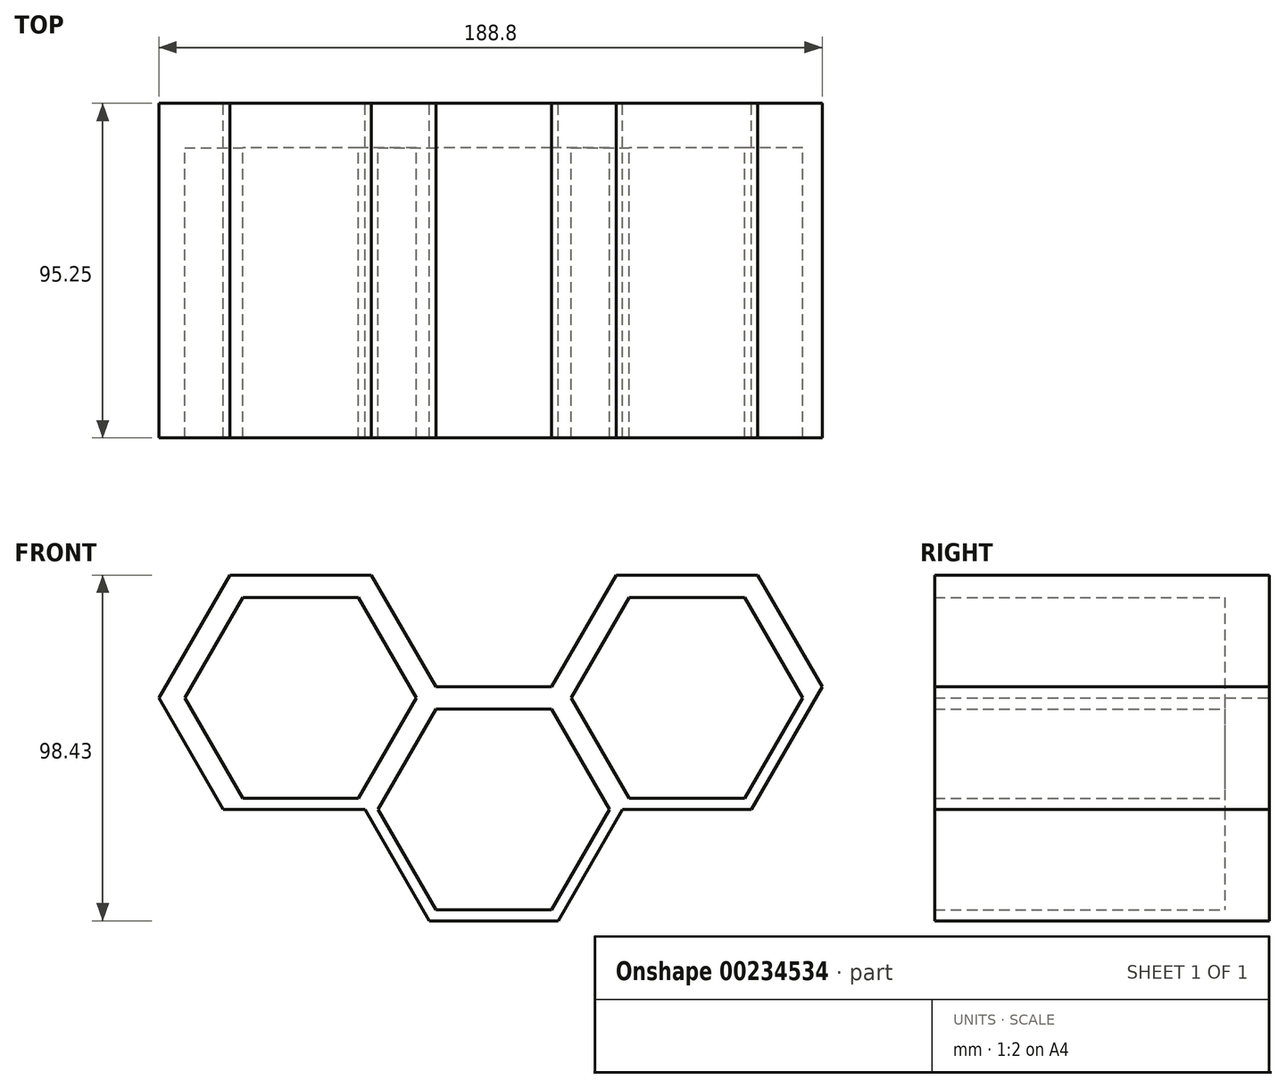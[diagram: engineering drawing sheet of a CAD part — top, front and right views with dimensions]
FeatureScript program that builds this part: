
annotation { "Feature Type Name" : "Feature", "Feature Type Description" : "" }
export const myFeature = defineFeature(function(context is Context, id is Id, definition is map)
    precondition{}
    {
        {
            var Q0;
            Q0=qCreatedBy(makeId("Front.planeOp"),FACE);
            var sketch = newSketch(context, id + "F0", { "sketchPlane" : qUnion([Q0])});
            skLineSegment(sketch, "E0.1", {"start": v(-114.26, 98.54) * mm, "end": v(-77.6, 98.54) * mm});
            skLineSegment(sketch, "E1.1", {"start": v(-169.26, 130.3) * mm, "end": v(-132.6, 130.3) * mm});
            skLineSegment(sketch, "E1.2", {"start": v(-132.6, 130.3) * mm, "end": v(-114.26, 98.54) * mm});
            skLineSegment(sketch, "E2.0", {"start": v(-77.6, 98.54) * mm, "end": v(-59.27, 130.3) * mm});
            skLineSegment(sketch, "E2.1", {"start": v(-59.27, 130.3) * mm, "end": v(-27.5, 130.3) * mm});
            skCircle(sketch, "E3.cCircle", {"center": v(-95.93, 130.3) * mm, "radius": 28.58 * mm, "construction": true});
            skLineSegment(sketch, "E3.0", {"start": v(-128.93, 130.3) * mm, "end": v(-112.43, 158.87) * mm});
            skLineSegment(sketch, "E3.1", {"start": v(-112.43, 158.87) * mm, "end": v(-79.43, 158.87) * mm});
            skLineSegment(sketch, "E3.2", {"start": v(-79.43, 158.87) * mm, "end": v(-62.94, 130.3) * mm});
            skLineSegment(sketch, "E3.3", {"start": v(-62.94, 130.3) * mm, "end": v(-79.43, 101.72) * mm});
            skLineSegment(sketch, "E3.4", {"start": v(-79.43, 101.72) * mm, "end": v(-112.43, 101.72) * mm});
            skLineSegment(sketch, "E3.5", {"start": v(-112.43, 101.72) * mm, "end": v(-128.93, 130.3) * mm});
            skPoint(sketch, "E3.0.midPoint", {"position": v(-120.68, 144.58) * mm});
            skCircle(sketch, "E4.cCircle", {"center": v(-95.93, 130.3) * mm, "radius": 31.75 * mm, "construction": true});
            skLineSegment(sketch, "E4.0", {"start": v(-132.6, 130.3) * mm, "end": v(-114.26, 162.04) * mm});
            skLineSegment(sketch, "E4.1", {"start": v(-114.26, 162.04) * mm, "end": v(-77.6, 162.04) * mm});
            skLineSegment(sketch, "E4.2", {"start": v(-77.6, 162.04) * mm, "end": v(-59.27, 130.3) * mm});
            skLineSegment(sketch, "E4.3", {"start": v(-59.27, 130.3) * mm, "end": v(-77.6, 98.54) * mm});
            skLineSegment(sketch, "E4.4", {"start": v(-77.6, 98.54) * mm, "end": v(-114.26, 98.54) * mm});
            skLineSegment(sketch, "E4.5", {"start": v(-114.26, 98.54) * mm, "end": v(-132.6, 130.3) * mm});
            skPoint(sketch, "E4.0.midPoint", {"position": v(-123.43, 146.17) * mm});
            skCircle(sketch, "E5.cCircle", {"center": v(-150.93, 162.04) * mm, "radius": 28.58 * mm, "construction": true});
            skLineSegment(sketch, "E5.0", {"start": v(-183.92, 162.04) * mm, "end": v(-167.42, 190.62) * mm});
            skLineSegment(sketch, "E5.1", {"start": v(-167.42, 190.62) * mm, "end": v(-134.43, 190.62) * mm});
            skLineSegment(sketch, "E5.2", {"start": v(-134.43, 190.62) * mm, "end": v(-117.93, 162.04) * mm});
            skLineSegment(sketch, "E5.3", {"start": v(-117.93, 162.04) * mm, "end": v(-134.43, 133.47) * mm});
            skLineSegment(sketch, "E5.4", {"start": v(-134.43, 133.47) * mm, "end": v(-167.42, 133.47) * mm});
            skLineSegment(sketch, "E5.5", {"start": v(-167.42, 133.47) * mm, "end": v(-183.92, 162.04) * mm});
            skPoint(sketch, "E5.0.midPoint", {"position": v(-175.67, 176.33) * mm});
            skCircle(sketch, "E6.cCircle", {"center": v(-150.93, 162.04) * mm, "radius": 31.75 * mm, "construction": true});
            skLineSegment(sketch, "E6.0", {"start": v(-187.59, 162.04) * mm, "end": v(-169.26, 193.8) * mm});
            skLineSegment(sketch, "E6.1", {"start": v(-169.26, 193.8) * mm, "end": v(-132.6, 193.8) * mm});
            skLineSegment(sketch, "E6.2", {"start": v(-132.6, 193.8) * mm, "end": v(-114.26, 162.04) * mm});
            skLineSegment(sketch, "E6.3", {"start": v(-114.26, 162.04) * mm, "end": v(-132.6, 130.3) * mm});
            skLineSegment(sketch, "E6.4", {"start": v(-132.6, 130.3) * mm, "end": v(-169.26, 130.3) * mm});
            skLineSegment(sketch, "E6.5", {"start": v(-169.26, 130.3) * mm, "end": v(-187.59, 162.04) * mm});
            skPoint(sketch, "E6.0.midPoint", {"position": v(-178.42, 177.92) * mm});
            skCircle(sketch, "E7.cCircle", {"center": v(-40.94, 162.04) * mm, "radius": 28.58 * mm, "construction": true});
            skLineSegment(sketch, "E7.0", {"start": v(-73.94, 162.04) * mm, "end": v(-57.44, 190.62) * mm});
            skLineSegment(sketch, "E7.1", {"start": v(-57.44, 190.62) * mm, "end": v(-24.44, 190.62) * mm});
            skLineSegment(sketch, "E7.2", {"start": v(-24.44, 190.62) * mm, "end": v(-7.94, 162.04) * mm});
            skLineSegment(sketch, "E7.3", {"start": v(-7.94, 162.04) * mm, "end": v(-24.44, 133.47) * mm});
            skLineSegment(sketch, "E7.4", {"start": v(-24.44, 133.47) * mm, "end": v(-57.44, 133.47) * mm});
            skLineSegment(sketch, "E7.5", {"start": v(-57.44, 133.47) * mm, "end": v(-73.94, 162.04) * mm});
            skCircle(sketch, "E8.cCircle", {"center": v(-40.94, 162.04) * mm, "radius": 31.75 * mm, "construction": true});
            skLineSegment(sketch, "E8.0", {"start": v(-77.6, 162.04) * mm, "end": v(-59.27, 193.8) * mm});
            skLineSegment(sketch, "E8.1", {"start": v(-59.27, 193.8) * mm, "end": v(-22.6, 193.8) * mm});
            skLineSegment(sketch, "E8.2", {"start": v(-22.6, 193.8) * mm, "end": v(-4.28, 162.04) * mm});
            skLineSegment(sketch, "E8.3", {"start": v(-4.28, 162.04) * mm, "end": v(-22.6, 130.3) * mm});
            skLineSegment(sketch, "E8.4", {"start": v(-22.6, 130.3) * mm, "end": v(-59.27, 130.3) * mm});
            skLineSegment(sketch, "E8.5", {"start": v(-59.27, 130.3) * mm, "end": v(-77.6, 162.04) * mm});
            skPoint(sketch, "E8.0.midPoint", {"position": v(-68.44, 177.92) * mm});
            skLineSegment(sketch, "E9.0", {"start": v(-22.6, 130.3) * mm, "end": v(-4.28, 162.04) * mm});
            skPoint(sketch, "E9.0.midPoint", {"position": v(-13.44, 146.17) * mm});
            skLineSegment(sketch, "E10", {"start": v(-2.45, 165.22) * mm, "end": v(-20.78, 196.97) * mm});
            skLineSegment(sketch, "E11", {"start": v(-20.78, 196.97) * mm, "end": v(-61.1, 196.97) * mm});
            skLineSegment(sketch, "E12", {"start": v(-61.1, 196.97) * mm, "end": v(-79.43, 165.22) * mm});
            skLineSegment(sketch, "E13", {"start": v(-171.09, 196.97) * mm, "end": v(-191.25, 162.04) * mm});
            skLineSegment(sketch, "E14", {"start": v(-191.25, 162.04) * mm, "end": v(-172.92, 130.3) * mm});
            skLineSegment(sketch, "E15", {"start": v(-171.09, 196.97) * mm, "end": v(-130.76, 196.97) * mm});
            skLineSegment(sketch, "E16", {"start": v(-130.76, 196.97) * mm, "end": v(-112.43, 165.22) * mm});
            skLineSegment(sketch, "E17", {"start": v(-112.43, 165.22) * mm, "end": v(-79.43, 165.22) * mm});
            skLineSegment(sketch, "E18", {"start": v(-57.44, 127.12) * mm, "end": v(-73.94, 98.54) * mm});
            skLineSegment(sketch, "E19", {"start": v(-24.44, 127.12) * mm, "end": v(-57.44, 127.12) * mm});
            skLineSegment(sketch, "E20", {"start": v(-22.6, 130.3) * mm, "end": v(-24.44, 127.12) * mm});
            skLineSegment(sketch, "E21", {"start": v(-73.94, 98.54) * mm, "end": v(-77.6, 98.54) * mm});
            skLineSegment(sketch, "E22", {"start": v(-169.26, 130.3) * mm, "end": v(-172.92, 130.3) * mm});
            skLineSegment(sketch, "E23", {"start": v(-2.45, 165.22) * mm, "end": v(-4.28, 162.04) * mm});
            skSolve(sketch);
        }
        {
            var Q0;
            Q0=makeQuery(id+"F0.imprint","IMPRINT",FACE,{"disambiguationData":[TD([[makeQuery(id+"F0.imprint","IMPRINT",EDGE,{"derivedFrom":sQuery(id+"F0.wireOp",EDGE,"E7.0")}),-1.0]])]});
            var Q1;
            Q1=makeQuery(id+"F0.imprint","IMPRINT",FACE,{"disambiguationData":[TD([[makeQuery(id+"F0.imprint","IMPRINT",EDGE,{"derivedFrom":sQuery(id+"F0.wireOp",EDGE,"ae29455d-c252-400a-b569-c5a1c48e1351.0")}),-1.0]])]});
            var Q2;
            Q2=makeQuery(id+"F0.imprint","IMPRINT",FACE,{"disambiguationData":[TD([[makeQuery(id+"F0.imprint","IMPRINT",EDGE,{"derivedFrom":sQuery(id+"F0.wireOp",EDGE,"cad1e4f3-bd43-45ec-b31a-1d5006939c94.0")}),-1.0]])]});
            var Q3;
            Q3=makeQuery(id+"F0.imprint","IMPRINT",FACE,{"disambiguationData":[TD([[makeQuery(id+"F0.imprint","IMPRINT",EDGE,{"derivedFrom":sQuery(id+"F0.wireOp",EDGE,"b43d4d8c-f78a-4ff8-8565-99a66ce6ec5f.0")}),-1.0]])]});
            var Q4;
            Q4=makeQuery(id+"F0.imprint","IMPRINT",FACE,{"disambiguationData":[TD([[makeQuery(id+"F0.imprint","IMPRINT",EDGE,{"derivedFrom":sQuery(id+"F0.wireOp",EDGE,"8c75d941-d110-4871-aa41-90a72d60fb2b.0")}),-1.0]])]});
            var Q5;
            Q5=makeQuery(id+"F0.imprint","IMPRINT",FACE,{"disambiguationData":[TD([[makeQuery(id+"F0.imprint","IMPRINT",EDGE,{"derivedFrom":sQuery(id+"F0.wireOp",EDGE,"258573fa-3544-418e-8bc5-5d37e5b8ba09.0")}),-1.0]])]});
            var Q6;
            Q6=makeQuery(id+"F0.imprint","IMPRINT",FACE,{"disambiguationData":[TD([[makeQuery(id+"F0.imprint","IMPRINT",EDGE,{"derivedFrom":sQuery(id+"F0.wireOp",EDGE,"0bf0733b-7d93-4c2e-8366-56d2cde24658.0")}),-1.0]])]});
            var Q7;
            Q7=makeQuery(id+"F0.imprint","IMPRINT",FACE,{"disambiguationData":[TD([[makeQuery(id+"F0.imprint","IMPRINT",EDGE,{"derivedFrom":sQuery(id+"F0.wireOp",EDGE,"93717492-86db-456f-ae55-f71e4e93837b.0")}),-1.0]])]});
            var Q8;
            Q8=makeQuery(id+"F0.imprint","IMPRINT",FACE,{"disambiguationData":[TD([[makeQuery(id+"F0.imprint","IMPRINT",EDGE,{"derivedFrom":sQuery(id+"F0.wireOp",EDGE,"f16ea8c9-6b67-4651-8441-f7eb3c0ce7d7.0")}),-1.0]])]});
            var Q9;
            Q9=makeQuery(id+"F0.imprint","IMPRINT",FACE,{"disambiguationData":[TD([[makeQuery(id+"F0.imprint","IMPRINT",EDGE,{"derivedFrom":sQuery(id+"F0.wireOp",EDGE,"E3.0")}),-1.0]])]});
            var Q10;
            Q10=makeQuery(id+"F0.imprint","IMPRINT",FACE,{"disambiguationData":[TD([[makeQuery(id+"F0.imprint","IMPRINT",EDGE,{"derivedFrom":sQuery(id+"F0.wireOp",EDGE,"0a91a14e-ea0c-483f-91eb-c48bd73cb0e6.0")}),-1.0]])]});
            var Q11;
            Q11=makeQuery(id+"F0.imprint","IMPRINT",FACE,{"disambiguationData":[TD([[makeQuery(id+"F0.imprint","IMPRINT",EDGE,{"derivedFrom":sQuery(id+"F0.wireOp",EDGE,"cbfd9497-f7fe-4f18-9288-d90aa8075d81.0")}),-1.0]])]});
            var Q12;
            Q12=makeQuery(id+"F0.imprint","IMPRINT",FACE,{"disambiguationData":[TD([[makeQuery(id+"F0.imprint","IMPRINT",EDGE,{"derivedFrom":sQuery(id+"F0.wireOp",EDGE,"6282d196-dd8f-4bb0-bca4-b9108e277473.0")}),-1.0]])]});
            var Q13;
            Q13=makeQuery(id+"F0.imprint","IMPRINT",FACE,{"disambiguationData":[TD([[makeQuery(id+"F0.imprint","IMPRINT",EDGE,{"derivedFrom":sQuery(id+"F0.wireOp",EDGE,"E5.0")}),-1.0]])]});
            var Q14;
            Q14=makeQuery(id+"F0.imprint","IMPRINT",FACE,{"disambiguationData":[TD([[makeQuery(id+"F0.imprint","IMPRINT",EDGE,{"derivedFrom":sQuery(id+"F0.wireOp",EDGE,"06c29831-6b25-410b-9247-4ee044b7735c.0")}),-1.0]])]});
            var Q15;
            Q15=makeQuery(id+"F0.imprint","IMPRINT",FACE,{"disambiguationData":[TD([[makeQuery(id+"F0.imprint","IMPRINT",EDGE,{"derivedFrom":sQuery(id+"F0.wireOp",EDGE,"b8eec94e-d97e-439b-aaac-63499233db4c.0")}),-1.0]])]});
            var Q16;
            Q16=makeQuery(id+"F0.imprint","IMPRINT",FACE,{"disambiguationData":[TD([[makeQuery(id+"F0.imprint","IMPRINT",EDGE,{"derivedFrom":sQuery(id+"F0.wireOp",EDGE,"2e929887-9bb9-4083-9cef-f9a6a24e8e46.0")}),-1.0]])]});
            var Q17;
            Q17=makeQuery(id+"F0.imprint","IMPRINT",FACE,{"disambiguationData":[TD([[makeQuery(id+"F0.imprint","IMPRINT",EDGE,{"derivedFrom":sQuery(id+"F0.wireOp",EDGE,"23671680-92ab-419e-a071-eb0943a5012b.0")}),-1.0]])]});
            var Q18;
            Q18=makeQuery(id+"F0.imprint","IMPRINT",FACE,{"disambiguationData":[TD([[makeQuery(id+"F0.imprint","IMPRINT",EDGE,{"derivedFrom":sQuery(id+"F0.wireOp",EDGE,"a1daa6ae-7864-4614-8fb9-3511dddc1266.0")}),-1.0]])]});
            var Q19;
            Q19=makeQuery(id+"F0.imprint","IMPRINT",FACE,{"disambiguationData":[TD([[makeQuery(id+"F0.imprint","IMPRINT",EDGE,{"derivedFrom":sQuery(id+"F0.wireOp",EDGE,"37efd634-c264-4683-8864-08b38c7986ca.0")}),-1.0]])]});
            var Q20;
            Q20=makeQuery(id+"F0.imprint","IMPRINT",FACE,{"disambiguationData":[TD([[makeQuery(id+"F0.imprint","IMPRINT",EDGE,{"derivedFrom":sQuery(id+"F0.wireOp",EDGE,"f2dd3995-374a-43c5-8725-4a87181dc8c5.0")}),-1.0]])]});
            var Q21;
            Q21=makeQuery(id+"F0.imprint","IMPRINT",FACE,{"disambiguationData":[TD([[makeQuery(id+"F0.imprint","IMPRINT",EDGE,{"derivedFrom":sQuery(id+"F0.wireOp",EDGE,"1f2aec04-a318-49b9-a42e-ea2fce35ed6c.0")}),-1.0]])]});
            var Q22;
            Q22=makeQuery(id+"F0.imprint","IMPRINT",FACE,{"disambiguationData":[TD([[makeQuery(id+"F0.imprint","IMPRINT",EDGE,{"derivedFrom":sQuery(id+"F0.wireOp",EDGE,"f97fdbdd-69fc-44f1-b8f7-f6a6a25558e6.0")}),-1.0]])]});
            var Q23;
            Q23=makeQuery(id+"F0.imprint","IMPRINT",FACE,{"disambiguationData":[TD([[makeQuery(id+"F0.imprint","IMPRINT",EDGE,{"derivedFrom":sQuery(id+"F0.wireOp",EDGE,"4e92e904-9607-490d-a429-b319c41500d9.0")}),-1.0]])]});
            var Q24;
            Q24=makeQuery(id+"F0.imprint","IMPRINT",FACE,{"disambiguationData":[TD([[makeQuery(id+"F0.imprint","IMPRINT",EDGE,{"derivedFrom":sQuery(id+"F0.wireOp",EDGE,"E5.0")}),1.0]])]});
            var Q25;
            Q25=makeQuery(id+"F0.imprint","IMPRINT",FACE,{"disambiguationData":[TD([[makeQuery(id+"F0.imprint","IMPRINT",EDGE,{"derivedFrom":sQuery(id+"F0.wireOp",EDGE,"1f2aec04-a318-49b9-a42e-ea2fce35ed6c.0")}),1.0]])]});
            var Q26;
            Q26=makeQuery(id+"F0.imprint","IMPRINT",FACE,{"disambiguationData":[TD([[makeQuery(id+"F0.imprint","IMPRINT",EDGE,{"derivedFrom":sQuery(id+"F0.wireOp",EDGE,"23671680-92ab-419e-a071-eb0943a5012b.0")}),1.0]])]});
            var Q27;
            Q27=makeQuery(id+"F0.imprint","IMPRINT",FACE,{"disambiguationData":[TD([[makeQuery(id+"F0.imprint","IMPRINT",EDGE,{"derivedFrom":sQuery(id+"F0.wireOp",EDGE,"2e929887-9bb9-4083-9cef-f9a6a24e8e46.0")}),1.0]])]});
            var Q28;
            Q28=makeQuery(id+"F0.imprint","IMPRINT",FACE,{"disambiguationData":[TD([[makeQuery(id+"F0.imprint","IMPRINT",EDGE,{"derivedFrom":sQuery(id+"F0.wireOp",EDGE,"4e92e904-9607-490d-a429-b319c41500d9.0")}),1.0]])]});
            var Q29;
            Q29=makeQuery(id+"F0.imprint","IMPRINT",FACE,{"disambiguationData":[TD([[makeQuery(id+"F0.imprint","IMPRINT",EDGE,{"derivedFrom":sQuery(id+"F0.wireOp",EDGE,"b43d4d8c-f78a-4ff8-8565-99a66ce6ec5f.0")}),1.0]])]});
            var Q30;
            Q30=makeQuery(id+"F0.imprint","IMPRINT",FACE,{"disambiguationData":[TD([[makeQuery(id+"F0.imprint","IMPRINT",EDGE,{"derivedFrom":sQuery(id+"F0.wireOp",EDGE,"ae29455d-c252-400a-b569-c5a1c48e1351.0")}),1.0]])]});
            var Q31;
            Q31=makeQuery(id+"F0.imprint","IMPRINT",FACE,{"disambiguationData":[TD([[makeQuery(id+"F0.imprint","IMPRINT",EDGE,{"derivedFrom":sQuery(id+"F0.wireOp",EDGE,"0a91a14e-ea0c-483f-91eb-c48bd73cb0e6.0")}),1.0]])]});
            var Q32;
            Q32=makeQuery(id+"F0.imprint","IMPRINT",FACE,{"disambiguationData":[TD([[makeQuery(id+"F0.imprint","IMPRINT",EDGE,{"derivedFrom":sQuery(id+"F0.wireOp",EDGE,"258573fa-3544-418e-8bc5-5d37e5b8ba09.0")}),1.0]])]});
            var Q33;
            Q33=makeQuery(id+"F0.imprint","IMPRINT",FACE,{"disambiguationData":[TD([[makeQuery(id+"F0.imprint","IMPRINT",EDGE,{"derivedFrom":sQuery(id+"F0.wireOp",EDGE,"cbfd9497-f7fe-4f18-9288-d90aa8075d81.0")}),1.0]])]});
            var Q34;
            Q34=makeQuery(id+"F0.imprint","IMPRINT",FACE,{"disambiguationData":[TD([[makeQuery(id+"F0.imprint","IMPRINT",EDGE,{"derivedFrom":sQuery(id+"F0.wireOp",EDGE,"f97fdbdd-69fc-44f1-b8f7-f6a6a25558e6.0")}),1.0]])]});
            var Q35;
            Q35=makeQuery(id+"F0.imprint","IMPRINT",FACE,{"disambiguationData":[TD([[makeQuery(id+"F0.imprint","IMPRINT",EDGE,{"derivedFrom":sQuery(id+"F0.wireOp",EDGE,"b8eec94e-d97e-439b-aaac-63499233db4c.0")}),1.0]])]});
            var Q36;
            Q36=makeQuery(id+"F0.imprint","IMPRINT",FACE,{"disambiguationData":[TD([[makeQuery(id+"F0.imprint","IMPRINT",EDGE,{"derivedFrom":sQuery(id+"F0.wireOp",EDGE,"8c75d941-d110-4871-aa41-90a72d60fb2b.0")}),1.0]])]});
            var Q37;
            Q37=makeQuery(id+"F0.imprint","IMPRINT",FACE,{"disambiguationData":[TD([[makeQuery(id+"F0.imprint","IMPRINT",EDGE,{"derivedFrom":sQuery(id+"F0.wireOp",EDGE,"f16ea8c9-6b67-4651-8441-f7eb3c0ce7d7.0")}),1.0]])]});
            var Q38;
            Q38=makeQuery(id+"F0.imprint","IMPRINT",FACE,{"disambiguationData":[TD([[makeQuery(id+"F0.imprint","IMPRINT",EDGE,{"derivedFrom":sQuery(id+"F0.wireOp",EDGE,"37efd634-c264-4683-8864-08b38c7986ca.0")}),1.0]])]});
            var Q39;
            Q39=makeQuery(id+"F0.imprint","IMPRINT",FACE,{"disambiguationData":[TD([[makeQuery(id+"F0.imprint","IMPRINT",EDGE,{"derivedFrom":sQuery(id+"F0.wireOp",EDGE,"E7.0")}),1.0]])]});
            var Q40;
            Q40=makeQuery(id+"F0.imprint","IMPRINT",FACE,{"disambiguationData":[TD([[makeQuery(id+"F0.imprint","IMPRINT",EDGE,{"derivedFrom":sQuery(id+"F0.wireOp",EDGE,"E3.0")}),1.0]])]});
            var Q41;
            Q41=makeQuery(id+"F0.imprint","IMPRINT",FACE,{"disambiguationData":[TD([[makeQuery(id+"F0.imprint","IMPRINT",EDGE,{"derivedFrom":sQuery(id+"F0.wireOp",EDGE,"0bf0733b-7d93-4c2e-8366-56d2cde24658.0")}),1.0]])]});
            var Q42;
            Q42=makeQuery(id+"F0.imprint","IMPRINT",FACE,{"disambiguationData":[TD([[makeQuery(id+"F0.imprint","IMPRINT",EDGE,{"derivedFrom":sQuery(id+"F0.wireOp",EDGE,"06c29831-6b25-410b-9247-4ee044b7735c.0")}),1.0]])]});
            var Q43;
            Q43=makeQuery(id+"F0.imprint","IMPRINT",FACE,{"disambiguationData":[TD([[makeQuery(id+"F0.imprint","IMPRINT",EDGE,{"derivedFrom":sQuery(id+"F0.wireOp",EDGE,"6282d196-dd8f-4bb0-bca4-b9108e277473.0")}),1.0]])]});
            var Q44;
            Q44=makeQuery(id+"F0.imprint","IMPRINT",FACE,{"disambiguationData":[TD([[makeQuery(id+"F0.imprint","IMPRINT",EDGE,{"derivedFrom":sQuery(id+"F0.wireOp",EDGE,"cad1e4f3-bd43-45ec-b31a-1d5006939c94.0")}),1.0]])]});
            var Q45;
            Q45=makeQuery(id+"F0.imprint","IMPRINT",FACE,{"disambiguationData":[TD([[makeQuery(id+"F0.imprint","IMPRINT",EDGE,{"derivedFrom":sQuery(id+"F0.wireOp",EDGE,"f2dd3995-374a-43c5-8725-4a87181dc8c5.0")}),1.0]])]});
            var Q46;
            Q46=makeQuery(id+"F0.imprint","IMPRINT",FACE,{"disambiguationData":[TD([[makeQuery(id+"F0.imprint","IMPRINT",EDGE,{"derivedFrom":sQuery(id+"F0.wireOp",EDGE,"a1daa6ae-7864-4614-8fb9-3511dddc1266.0")}),1.0]])]});
            var Q47;
            Q47=makeQuery(id+"F0.imprint","IMPRINT",FACE,{"disambiguationData":[TD([[makeQuery(id+"F0.imprint","IMPRINT",EDGE,{"derivedFrom":sQuery(id+"F0.wireOp",EDGE,"93717492-86db-456f-ae55-f71e4e93837b.0")}),1.0]])]});
            extrude(context, id + "F1", {"entities" : qUnion([Q0, Q1, Q2, Q3, Q4, Q5, Q6, Q7, Q8, Q9, Q10, Q11, Q12, Q13, Q14, Q15, Q16, Q17, Q18, Q19, Q20, Q21, Q22, Q23, Q24, Q25, Q26, Q27, Q28, Q29, Q30, Q31, Q32, Q33, Q34, Q35, Q36, Q37, Q38, Q39, Q40, Q41, Q42, Q43, Q44, Q45, Q46, Q47]), "depth" : 12.7 * mm});
        }
        {
            var Q0;
            Q0=makeQuery(id+"F0.imprint","IMPRINT",FACE,{"disambiguationData":[TD([[makeQuery(id+"F0.imprint","IMPRINT",EDGE,{"derivedFrom":sQuery(id+"F0.wireOp",EDGE,"8c75d941-d110-4871-aa41-90a72d60fb2b.0")}),1.0]])]});
            var Q1;
            Q1=makeQuery(id+"F0.imprint","IMPRINT",FACE,{"disambiguationData":[TD([[makeQuery(id+"F0.imprint","IMPRINT",EDGE,{"derivedFrom":sQuery(id+"F0.wireOp",EDGE,"b8eec94e-d97e-439b-aaac-63499233db4c.0")}),1.0]])]});
            var Q2;
            Q2=makeQuery(id+"F0.imprint","IMPRINT",FACE,{"disambiguationData":[TD([[makeQuery(id+"F0.imprint","IMPRINT",EDGE,{"derivedFrom":sQuery(id+"F0.wireOp",EDGE,"cad1e4f3-bd43-45ec-b31a-1d5006939c94.0")}),1.0]])]});
            var Q3;
            Q3=makeQuery(id+"F0.imprint","IMPRINT",FACE,{"disambiguationData":[TD([[makeQuery(id+"F0.imprint","IMPRINT",EDGE,{"derivedFrom":sQuery(id+"F0.wireOp",EDGE,"E7.0")}),1.0]])]});
            var Q4;
            Q4=makeQuery(id+"F0.imprint","IMPRINT",FACE,{"disambiguationData":[TD([[makeQuery(id+"F0.imprint","IMPRINT",EDGE,{"derivedFrom":sQuery(id+"F0.wireOp",EDGE,"E3.0")}),1.0]])]});
            var Q5;
            Q5=makeQuery(id+"F0.imprint","IMPRINT",FACE,{"disambiguationData":[TD([[makeQuery(id+"F0.imprint","IMPRINT",EDGE,{"derivedFrom":sQuery(id+"F0.wireOp",EDGE,"E5.0")}),1.0]])]});
            var Q6;
            Q6=makeQuery(id+"F0.imprint","IMPRINT",FACE,{"disambiguationData":[TD([[makeQuery(id+"F0.imprint","IMPRINT",EDGE,{"derivedFrom":sQuery(id+"F0.wireOp",EDGE,"4e92e904-9607-490d-a429-b319c41500d9.0")}),1.0]])]});
            var Q7;
            Q7=makeQuery(id+"F0.imprint","IMPRINT",FACE,{"disambiguationData":[TD([[makeQuery(id+"F0.imprint","IMPRINT",EDGE,{"derivedFrom":sQuery(id+"F0.wireOp",EDGE,"a1daa6ae-7864-4614-8fb9-3511dddc1266.0")}),1.0]])]});
            var Q8;
            Q8=makeQuery(id+"F0.imprint","IMPRINT",FACE,{"disambiguationData":[TD([[makeQuery(id+"F0.imprint","IMPRINT",EDGE,{"derivedFrom":sQuery(id+"F0.wireOp",EDGE,"93717492-86db-456f-ae55-f71e4e93837b.0")}),1.0]])]});
            var Q9;
            Q9=makeQuery(id+"F0.imprint","IMPRINT",FACE,{"disambiguationData":[TD([[makeQuery(id+"F0.imprint","IMPRINT",EDGE,{"derivedFrom":sQuery(id+"F0.wireOp",EDGE,"258573fa-3544-418e-8bc5-5d37e5b8ba09.0")}),1.0]])]});
            var Q10;
            Q10=makeQuery(id+"F0.imprint","IMPRINT",FACE,{"disambiguationData":[TD([[makeQuery(id+"F0.imprint","IMPRINT",EDGE,{"derivedFrom":sQuery(id+"F0.wireOp",EDGE,"f2dd3995-374a-43c5-8725-4a87181dc8c5.0")}),1.0]])]});
            var Q11;
            Q11=makeQuery(id+"F0.imprint","IMPRINT",FACE,{"disambiguationData":[TD([[makeQuery(id+"F0.imprint","IMPRINT",EDGE,{"derivedFrom":sQuery(id+"F0.wireOp",EDGE,"23671680-92ab-419e-a071-eb0943a5012b.0")}),1.0]])]});
            var Q12;
            Q12=makeQuery(id+"F0.imprint","IMPRINT",FACE,{"disambiguationData":[TD([[makeQuery(id+"F0.imprint","IMPRINT",EDGE,{"derivedFrom":sQuery(id+"F0.wireOp",EDGE,"06c29831-6b25-410b-9247-4ee044b7735c.0")}),1.0]])]});
            var Q13;
            Q13=makeQuery(id+"F0.imprint","IMPRINT",FACE,{"disambiguationData":[TD([[makeQuery(id+"F0.imprint","IMPRINT",EDGE,{"derivedFrom":sQuery(id+"F0.wireOp",EDGE,"ae29455d-c252-400a-b569-c5a1c48e1351.0")}),1.0]])]});
            var Q14;
            Q14=makeQuery(id+"F0.imprint","IMPRINT",FACE,{"disambiguationData":[TD([[makeQuery(id+"F0.imprint","IMPRINT",EDGE,{"derivedFrom":sQuery(id+"F0.wireOp",EDGE,"f97fdbdd-69fc-44f1-b8f7-f6a6a25558e6.0")}),1.0]])]});
            var Q15;
            Q15=makeQuery(id+"F0.imprint","IMPRINT",FACE,{"disambiguationData":[TD([[makeQuery(id+"F0.imprint","IMPRINT",EDGE,{"derivedFrom":sQuery(id+"F0.wireOp",EDGE,"2e929887-9bb9-4083-9cef-f9a6a24e8e46.0")}),1.0]])]});
            var Q16;
            Q16=makeQuery(id+"F0.imprint","IMPRINT",FACE,{"disambiguationData":[TD([[makeQuery(id+"F0.imprint","IMPRINT",EDGE,{"derivedFrom":sQuery(id+"F0.wireOp",EDGE,"0a91a14e-ea0c-483f-91eb-c48bd73cb0e6.0")}),1.0]])]});
            var Q17;
            Q17=makeQuery(id+"F0.imprint","IMPRINT",FACE,{"disambiguationData":[TD([[makeQuery(id+"F0.imprint","IMPRINT",EDGE,{"derivedFrom":sQuery(id+"F0.wireOp",EDGE,"37efd634-c264-4683-8864-08b38c7986ca.0")}),1.0]])]});
            var Q18;
            Q18=makeQuery(id+"F0.imprint","IMPRINT",FACE,{"disambiguationData":[TD([[makeQuery(id+"F0.imprint","IMPRINT",EDGE,{"derivedFrom":sQuery(id+"F0.wireOp",EDGE,"cbfd9497-f7fe-4f18-9288-d90aa8075d81.0")}),1.0]])]});
            var Q19;
            Q19=makeQuery(id+"F0.imprint","IMPRINT",FACE,{"disambiguationData":[TD([[makeQuery(id+"F0.imprint","IMPRINT",EDGE,{"derivedFrom":sQuery(id+"F0.wireOp",EDGE,"6282d196-dd8f-4bb0-bca4-b9108e277473.0")}),1.0]])]});
            var Q20;
            Q20=makeQuery(id+"F0.imprint","IMPRINT",FACE,{"disambiguationData":[TD([[makeQuery(id+"F0.imprint","IMPRINT",EDGE,{"derivedFrom":sQuery(id+"F0.wireOp",EDGE,"0bf0733b-7d93-4c2e-8366-56d2cde24658.0")}),1.0]])]});
            var Q21;
            Q21=makeQuery(id+"F0.imprint","IMPRINT",FACE,{"disambiguationData":[TD([[makeQuery(id+"F0.imprint","IMPRINT",EDGE,{"derivedFrom":sQuery(id+"F0.wireOp",EDGE,"b43d4d8c-f78a-4ff8-8565-99a66ce6ec5f.0")}),1.0]])]});
            var Q22;
            Q22=makeQuery(id+"F0.imprint","IMPRINT",FACE,{"disambiguationData":[TD([[makeQuery(id+"F0.imprint","IMPRINT",EDGE,{"derivedFrom":sQuery(id+"F0.wireOp",EDGE,"f16ea8c9-6b67-4651-8441-f7eb3c0ce7d7.0")}),1.0]])]});
            var Q23;
            Q23=makeQuery(id+"F0.imprint","IMPRINT",FACE,{"disambiguationData":[TD([[makeQuery(id+"F0.imprint","IMPRINT",EDGE,{"derivedFrom":sQuery(id+"F0.wireOp",EDGE,"1f2aec04-a318-49b9-a42e-ea2fce35ed6c.0")}),1.0]])]});
            var Q24;
            {var subQ6=sQuery(id+"F0.wireOp",EDGE,"16495d92-3f2e-4778-aa2a-097d1cd616f4.3");Q24=makeQuery(id+"F0.imprint","IMPRINT",FACE,{"disambiguationData":[TD([[makeQuery(id+"F0.imprint","IMPRINT",EDGE,{"derivedFrom":subQ6}),1.0]])]});}
            var Q25;
            Q25=makeQuery(id+"F0.imprint","IMPRINT",FACE,{"disambiguationData":[TD([[makeQuery(id+"F0.imprint","IMPRINT",EDGE,{"derivedFrom":sQuery(id+"F0.wireOp",EDGE,"16495d92-3f2e-4778-aa2a-097d1cd616f4.1")}),1.0]])]});
            var Q26;
            Q26=makeQuery(id+"F0.imprint","IMPRINT",FACE,{"disambiguationData":[TD([[makeQuery(id+"F0.imprint","IMPRINT",EDGE,{"derivedFrom":sQuery(id+"F0.wireOp",EDGE,"E4.1")}),1.0]])]});
            var Q27;
            {var subQ1=sQuery(id+"F0.wireOp",EDGE,"E4.3");Q27=makeQuery(id+"F0.imprint","IMPRINT",FACE,{"disambiguationData":[TD([[makeQuery(id+"F0.imprint","IMPRINT",EDGE,{"derivedFrom":subQ1}),1.0]])]});}
            extrude(context, id + "F2", {"entities" : qUnion([Q0, Q1, Q2, Q3, Q4, Q5, Q6, Q7, Q8, Q9, Q10, Q11, Q12, Q13, Q14, Q15, Q16, Q17, Q18, Q19, Q20, Q21, Q22, Q23, Q24, Q25, Q26, Q27]), "operationType" : NewBodyOperationType.ADD, "depth" : 95.25 * mm});
        }
    });
